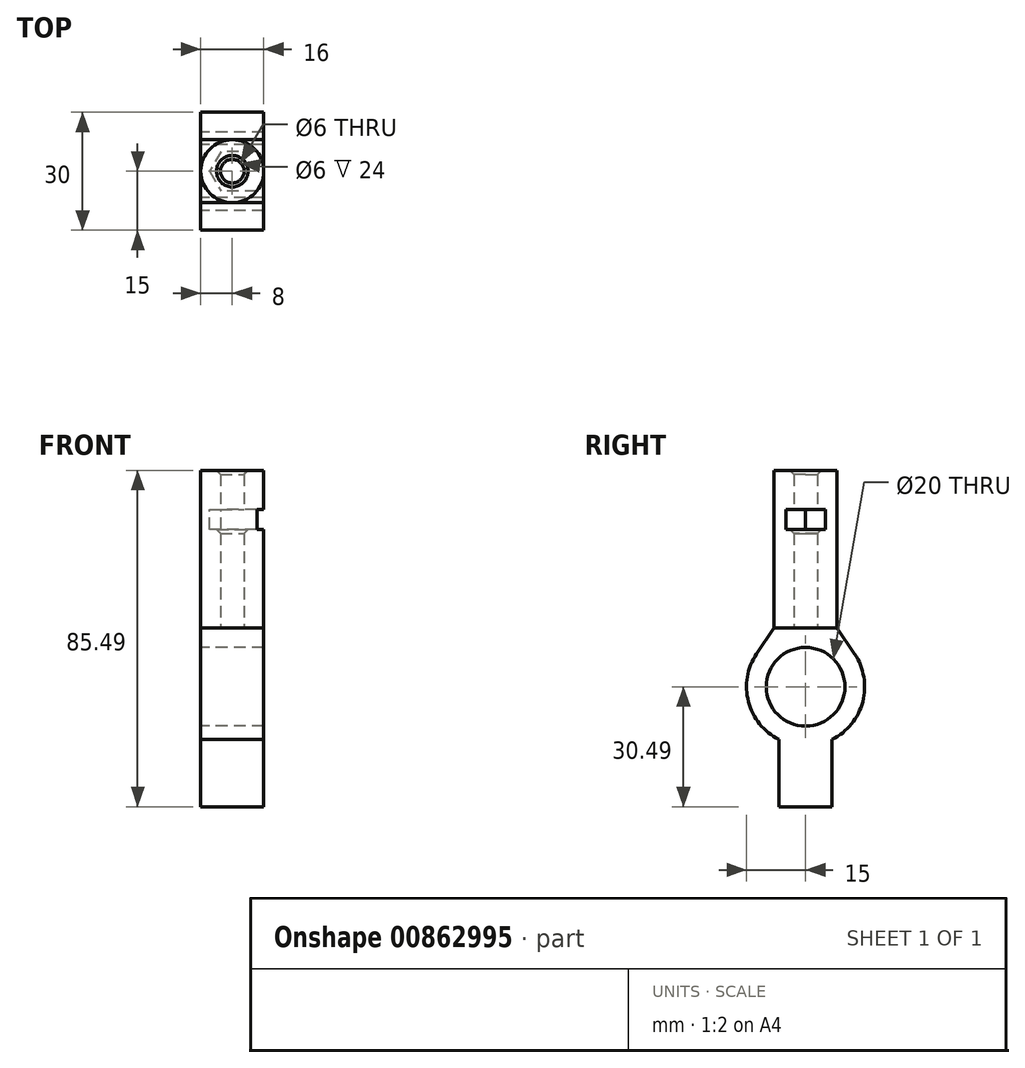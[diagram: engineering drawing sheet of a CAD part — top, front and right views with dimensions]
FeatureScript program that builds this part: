
annotation { "Feature Type Name" : "Feature", "Feature Type Description" : "" }
export const myFeature = defineFeature(function(context is Context, id is Id, definition is map)
    precondition{}
    {
        {
            var Q0;
            Q0=qCreatedBy(makeId("Top.planeOp"),FACE);
            var sketch = newSketch(context, id + "F0", { "sketchPlane" : qUnion([Q0])});
            skCircle(sketch, "E0", {"center": v(0, 0) * mm, "radius": 8 * mm});
            skCircle(sketch, "E1", {"center": v(0, 0) * mm, "radius": 3 * mm});
            skSolve(sketch);
        }
        {
            var Q0;
            Q0 = qSketchRegion(id + "F0", true);
            extrude(context, id + "F1", {"entities" : qUnion([Q0]), "depth" : 40 * mm, "offsetDistance" : 25 * mm});
        }
        {
            var Q0;
            Q0=qCreatedBy(makeId("Right.planeOp"),FACE);
            var sketch = newSketch(context, id + "F2", { "sketchPlane" : qUnion([Q0])});
            skLineSegment(sketch, "E2", {"start": v(0, 0) * mm, "end": v(0, -30) * mm, "construction": true});
            skCircle(sketch, "E3", {"center": v(0, -15) * mm, "radius": 15 * mm});
            skLineSegment(sketch, "E4.0", {"start": v(-8, 0) * mm, "end": v(8, 0) * mm});
            skCircle(sketch, "E5.0", {"center": v(0, -15) * mm, "radius": 10 * mm});
            skLineSegment(sketch, "E6", {"start": v(8, 0) * mm, "end": v(12.46, -6.64) * mm});
            skLineSegment(sketch, "E7.MirrorCS", {"start": v(-8, 0) * mm, "end": v(-12.46, -6.64) * mm});
            skLineSegment(sketch, "E8.bottom", {"start": v(6.76, -45.5) * mm, "end": v(-6.76, -45.5) * mm});
            skLineSegment(sketch, "E8.top", {"start": v(6.76, -14.5) * mm, "end": v(-6.76, -14.5) * mm});
            skLineSegment(sketch, "E8.left", {"start": v(6.76, -45.5) * mm, "end": v(6.76, -14.5) * mm});
            skLineSegment(sketch, "E8.right", {"start": v(-6.76, -45.5) * mm, "end": v(-6.76, -14.5) * mm});
            skPoint(sketch, "E8.middle", {"position": v(0, -30) * mm});
            skSolve(sketch);
        }
        {
            var Q0;
            Q0 = qSketchRegion(id + "F2", true);
            extrude(context, id + "F3", {"entities" : qUnion([Q0]), "operationType" : NewBodyOperationType.ADD, "depth" : 16 * mm, "offsetDistance" : 25 * mm, "symmetric" : true});
        }
        {
            var Q0;
            Q0=qCreatedBy(makeId("Right.planeOp"),FACE);
            var sketch = newSketch(context, id + "F4", { "sketchPlane" : qUnion([Q0])});
            skLineSegment(sketch, "E9.bottom", {"start": v(5, 25) * mm, "end": v(-5, 25) * mm});
            skLineSegment(sketch, "E9.top", {"start": v(5, 30) * mm, "end": v(-5, 30) * mm});
            skLineSegment(sketch, "E9.left", {"start": v(5, 25) * mm, "end": v(5, 30) * mm});
            skLineSegment(sketch, "E9.right", {"start": v(-5, 25) * mm, "end": v(-5, 30) * mm});
            skPoint(sketch, "E9.middle", {"position": v(0, 27.5) * mm});
            skSolve(sketch);
        }
        {
            var Q0;
            Q0 = qSketchRegion(id + "F4", true);
            extrude(context, id + "F5", {"entities" : qUnion([Q0]), "operationType" : NewBodyOperationType.REMOVE, "endBound" : BoundingType.THROUGH_ALL, "depth" : 25 * mm, "offsetDistance" : 25 * mm});
        }
        {
            var Q0;
            Q0=makeQuery(id+"F5.boolean.opBoolean","COPY",FACE,{"derivedFrom":makeQuery(id+"F5.opExtrude","SWEPT_FACE",FACE,{"disambiguationData":[OSD([sQuery(id+"F4.wireOp",EDGE,"E9.top")])]})});
            var sketch = newSketch(context, id + "F6", { "sketchPlane" : qUnion([Q0])});
            skCircle(sketch, "E10.cCircle", {"center": v(0, 0) * mm, "radius": 5 * mm, "construction": true});
            skLineSegment(sketch, "E10.0", {"start": v(2.89, -5) * mm, "end": v(-2.89, -5) * mm});
            skLineSegment(sketch, "E10.1", {"start": v(-2.89, -5) * mm, "end": v(-5.77, 0) * mm});
            skLineSegment(sketch, "E10.2", {"start": v(-5.77, 0) * mm, "end": v(-2.89, 5) * mm});
            skLineSegment(sketch, "E10.3", {"start": v(-2.89, 5) * mm, "end": v(2.89, 5) * mm});
            skLineSegment(sketch, "E10.4", {"start": v(2.89, 5) * mm, "end": v(5.77, 0) * mm});
            skLineSegment(sketch, "E10.5", {"start": v(5.77, 0) * mm, "end": v(2.89, -5) * mm});
            skPoint(sketch, "E10.0.midPoint", {"position": v(0, -5) * mm});
            skSolve(sketch);
        }
        {
            var Q0;
            Q0 = qSketchRegion(id + "F6", true);
            var Q1;
            Q1=makeQuery(id+"F5.boolean.opBoolean","COPY",FACE,{"derivedFrom":makeQuery(id+"F5.opExtrude","SWEPT_FACE",FACE,{"disambiguationData":[OSD([sQuery(id+"F4.wireOp",EDGE,"E9.bottom")])]})});
            extrude(context, id + "F7", {"entities" : qUnion([Q0]), "operationType" : NewBodyOperationType.REMOVE, "endBound" : BoundingType.UP_TO_SURFACE, "depth" : 25 * mm, "endBoundEntityFace" : qUnion([Q1]), "offsetDistance" : 25 * mm});
        }
        {
            var Q0;
            Q0=makeQuery(id+"F1.opExtrude","CAP_EDGE",EDGE,{"disambiguationData":[OSD([sQuery(id+"F0.wireOp",EDGE,"E1")])],"isStart":false});
            var Q1;
            Q1=makeQuery(id+"F7.boolean.opBoolean","INTERSECT",EDGE,{"derivedFrom":[makeQuery(id+"F1.opExtrude","SWEPT_FACE",FACE,{"disambiguationData":[OSD([sQuery(id+"F0.wireOp",EDGE,"E1")])]}),makeQuery(id+"F7.opExtrude","CAP_FACE",FACE,{"disambiguationData":[OSD([sQuery(id+"F6.wireOp",EDGE,"E10.0"),sQuery(id+"F6.wireOp",EDGE,"E10.1"),sQuery(id+"F6.wireOp",EDGE,"E10.2"),sQuery(id+"F6.wireOp",EDGE,"E10.3"),sQuery(id+"F6.wireOp",EDGE,"E10.4"),sQuery(id+"F6.wireOp",EDGE,"E10.5")])],"isStart":false})]});
            chamfer(context, id + "F8", {"entities" : qUnion([Q0, Q1]), "width" : 1 * mm, "tangentPropagation" : true});
        }
    });
